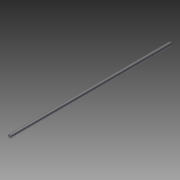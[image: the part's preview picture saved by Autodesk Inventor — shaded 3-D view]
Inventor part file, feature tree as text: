
AUTODESK INVENTOR PART (.ipt)
format: ipt  version: 2014 (Build 180170000, 170)  size: 73,728 bytes
history: native  units: in
note: dims shown in document units (in); Inventor stores cm internally (conversion verified against a paired STEP export)
features: extrude x1, other x1, thread x1, imported_body x1
ambient origin geometry x8: Origin, YZ Plane, XZ Plane, XY Plane, X Axis, Y Axis, Z Axis, Center Point
bodies: Body1 (feature_tree)
feature tree (4):
  extrude  "Extrude1"  Depth=1.0in TaperAngle=0.0deg
  other  "Ametek-BFWFSR-037-0068-18_screw.ipt1"
  thread  "Thread1"  [1 undecoded]
  imported_body  "Base1"
note: 1 required parameter value undecoded (feature->parameter linkage not recoverable at this tier; creation-order binding heuristic only, values carry confidence <= 0.55)
